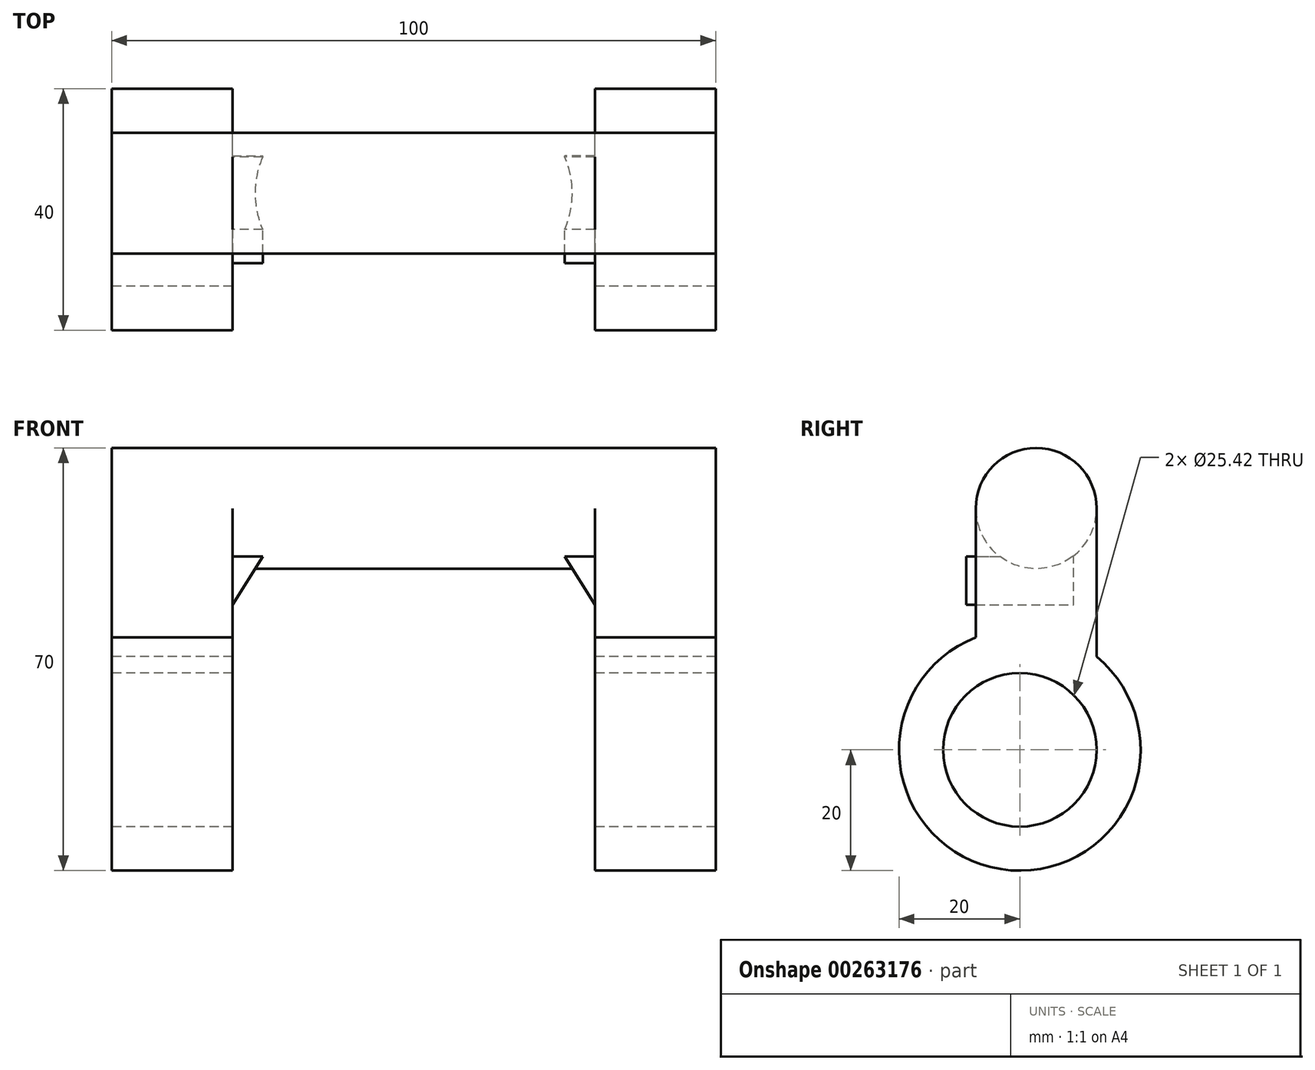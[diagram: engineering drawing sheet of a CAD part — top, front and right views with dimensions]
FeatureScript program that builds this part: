
annotation { "Feature Type Name" : "Feature", "Feature Type Description" : "" }
export const myFeature = defineFeature(function(context is Context, id is Id, definition is map)
    precondition{}
    {
        {
            assignVariable(context, id + "F0", {"name" : "Rin", "anyValue" : 12.7});
        }
        {
            assignVariable(context, id + "F1", {"name" : "long", "anyValue" : 100});
        }
        {
            var Q0;
            Q0=qCreatedBy(makeId("Right.planeOp"),FACE);
            var sketch = newSketch(context, id + "F2", { "sketchPlane" : qUnion([Q0])});
            skCircle(sketch, "E0", {"center": v(0, 0) * mm, "radius": 12.7 * mm});
            skCircle(sketch, "E1", {"center": v(0, 0) * mm, "radius": 20 * mm});
            skLineSegment(sketch, "E2.bottom", {"start": v(12.7, 0) * mm, "end": v(-7.3, 0) * mm});
            skLineSegment(sketch, "E2.left", {"start": v(12.7, 0) * mm, "end": v(12.7, 40) * mm});
            skLineSegment(sketch, "E2.right", {"start": v(-7.3, 0) * mm, "end": v(-7.3, 40) * mm});
            skCircle(sketch, "E3", {"center": v(2.7, 40) * mm, "radius": 10 * mm});
            skSolve(sketch);
        }
        {
            var Q0;
            {var subQ0=sQuery(id+"F2.wireOp",EDGE,"E3");var subQ1=makeQuery(id+"F2.imprint","INTERSECT",VERTEX,{"derivedFrom":[sQuery(id+"F2.wireOp",EDGE,"E2.left"),subQ0]});Q0=makeQuery(id+"F2.imprint","IMPRINT",FACE,{"disambiguationData":[TD([[makeQuery(id+"F2.imprint","IMPRINT",EDGE,{"disambiguationData":[TD([[subQ1,-1.0]])],"derivedFrom":subQ0}),1.0]])]});}
            var Q1;
            {var subQ0=sQuery(id+"F2.wireOp",EDGE,"E2.left");var subQ1=sQuery(id+"F2.wireOp",EDGE,"E1");var subQ2=makeQuery(id+"F2.imprint","INTERSECT",VERTEX,{"derivedFrom":[subQ1,subQ0]});Q1=makeQuery(id+"F2.imprint","IMPRINT",FACE,{"disambiguationData":[TD([[makeQuery(id+"F2.imprint","IMPRINT",EDGE,{"disambiguationData":[TD([[subQ2,-1.0]])],"derivedFrom":subQ1}),-1.0]])]});}
            var Q2;
            {var subQ0=sQuery(id+"F2.wireOp",EDGE,"E2.left");var subQ6=sQuery(id+"F2.wireOp",EDGE,"E1");var subQ7=makeQuery(id+"F2.imprint","INTERSECT",VERTEX,{"derivedFrom":[subQ6,subQ0]});Q2=makeQuery(id+"F2.imprint","IMPRINT",FACE,{"disambiguationData":[TD([[makeQuery(id+"F2.imprint","IMPRINT",EDGE,{"disambiguationData":[TD([[subQ7,-1.0]])],"derivedFrom":subQ6}),1.0]])]});}
            var Q3;
            {var subQ0=sQuery(id+"F2.wireOp",EDGE,"E2.left");var subQ6=sQuery(id+"F2.wireOp",EDGE,"E1");var subQ7=makeQuery(id+"F2.imprint","INTERSECT",VERTEX,{"derivedFrom":[subQ6,subQ0]});Q3=makeQuery(id+"F2.imprint","IMPRINT",FACE,{"disambiguationData":[TD([[makeQuery(id+"F2.imprint","IMPRINT",EDGE,{"disambiguationData":[TD([[subQ7,1.0]])],"derivedFrom":subQ6}),1.0]])]});}
            extrude(context, id + "F3", {"entities" : qUnion([Q0, Q1, Q2, Q3]), "depth" : 0.5 * (getVariable(context, 'long')) * mm, "hasSecondDirection" : true, "secondDirectionOppositeDirection" : true, "secondDirectionDepth" : 0.5 * (getVariable(context, 'long')) * mm});
        }
        {
            var Q0;
            {var subQ0=sQuery(id+"F2.wireOp",EDGE,"E2.left");var subQ1=sQuery(id+"F2.wireOp",EDGE,"E1");var subQ2=makeQuery(id+"F2.imprint","INTERSECT",VERTEX,{"derivedFrom":[subQ1,subQ0]});Q0=makeQuery(id+"F2.imprint","IMPRINT",FACE,{"disambiguationData":[TD([[makeQuery(id+"F2.imprint","IMPRINT",EDGE,{"disambiguationData":[TD([[subQ2,-1.0]])],"derivedFrom":subQ1}),-1.0]])]});}
            extrude(context, id + "F4", {"entities" : qUnion([Q0]), "operationType" : NewBodyOperationType.REMOVE, "oppositeDirection" : true, "depth" : (0.3 * getVariable(context, 'long')) * mm, "hasSecondDirection" : true, "secondDirectionOppositeDirection" : false, "secondDirectionDepth" : (0.3 * getVariable(context, 'long')) * mm});
        }
        {
            var Q0;
            {var subQ0=sQuery(id+"F2.wireOp",EDGE,"E2.left");var subQ6=sQuery(id+"F2.wireOp",EDGE,"E1");var subQ7=makeQuery(id+"F2.imprint","INTERSECT",VERTEX,{"derivedFrom":[subQ6,subQ0]});Q0=makeQuery(id+"F2.imprint","IMPRINT",FACE,{"disambiguationData":[TD([[makeQuery(id+"F2.imprint","IMPRINT",EDGE,{"disambiguationData":[TD([[subQ7,1.0]])],"derivedFrom":subQ6}),1.0]])]});}
            var Q1;
            {var subQ0=sQuery(id+"F2.wireOp",EDGE,"E2.left");var subQ6=sQuery(id+"F2.wireOp",EDGE,"E1");var subQ7=makeQuery(id+"F2.imprint","INTERSECT",VERTEX,{"derivedFrom":[subQ6,subQ0]});Q1=makeQuery(id+"F2.imprint","IMPRINT",FACE,{"disambiguationData":[TD([[makeQuery(id+"F2.imprint","IMPRINT",EDGE,{"disambiguationData":[TD([[subQ7,-1.0]])],"derivedFrom":subQ6}),1.0]])]});}
            extrude(context, id + "F5", {"entities" : qUnion([Q0, Q1]), "operationType" : NewBodyOperationType.REMOVE, "oppositeDirection" : true, "depth" : (0.3 * getVariable(context, 'long')) * mm, "hasSecondDirection" : true, "secondDirectionOppositeDirection" : false, "secondDirectionDepth" : (0.3 * getVariable(context, 'long')) * mm});
        }
        {
            var Q0;
            Q0=qCreatedBy(makeId("Front.planeOp"),FACE);
            var sketch = newSketch(context, id + "F6", { "sketchPlane" : qUnion([Q0])});
            skLineSegment(sketch, "E4", {"start": v(0, 0) * mm, "end": v(-50, 0) * mm});
            skLineSegment(sketch, "E5", {"start": v(-50, 0) * mm, "end": v(-50, 32) * mm});
            skLineSegment(sketch, "E6", {"start": v(-50, 32) * mm, "end": v(-25, 32) * mm});
            skLineSegment(sketch, "E7", {"start": v(-30, 0) * mm, "end": v(-30, 24) * mm});
            skLineSegment(sketch, "E8", {"start": v(-30, 24) * mm, "end": v(-25, 32) * mm});
            skLineSegment(sketch, "E9", {"start": v(-30, 24) * mm, "end": v(-30, 32) * mm});
            skLineSegment(sketch, "E10", {"start": v(0, 0) * mm, "end": v(50, 0) * mm});
            skLineSegment(sketch, "E11", {"start": v(50, 0) * mm, "end": v(50, 32) * mm});
            skLineSegment(sketch, "E12", {"start": v(50, 32) * mm, "end": v(25, 32) * mm});
            skLineSegment(sketch, "E13", {"start": v(25, 32) * mm, "end": v(30, 24) * mm});
            skLineSegment(sketch, "E14", {"start": v(30, 24) * mm, "end": v(30, 0) * mm});
            skLineSegment(sketch, "E15", {"start": v(30, 24) * mm, "end": v(30, 32) * mm});
            skSolve(sketch);
        }
        {
            var Q0;
            {var subQ0=sQuery(id+"F6.wireOp",EDGE,"E13");Q0=makeQuery(id+"F6.imprint","IMPRINT",FACE,{"disambiguationData":[TD([[makeQuery(id+"F6.imprint","IMPRINT",EDGE,{"derivedFrom":subQ0}),1.0]])]});}
            var Q1;
            {var subQ0=sQuery(id+"F6.wireOp",EDGE,"E8");Q1=makeQuery(id+"F6.imprint","IMPRINT",FACE,{"disambiguationData":[TD([[makeQuery(id+"F6.imprint","IMPRINT",EDGE,{"derivedFrom":subQ0}),1.0]])]});}
            extrude(context, id + "F7", {"entities" : qUnion([Q0, Q1]), "operationType" : NewBodyOperationType.ADD, "depth" : 0.7 * (getVariable(context, 'Rin')) * mm, "hasSecondDirection" : true, "secondDirectionOppositeDirection" : true, "secondDirectionDepth" : 0.7 * (getVariable(context, 'Rin')) * mm});
        }
    });
